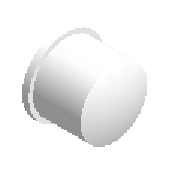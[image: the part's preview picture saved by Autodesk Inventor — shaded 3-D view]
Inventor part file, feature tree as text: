
AUTODESK INVENTOR PART (.ipt)
format: ipt  version: 2023.1 (Build 271208000, 208)  size: 160,256 bytes
history: native  units: mm (DEFAULTED — no unit token found)
features: other x4, revolve x2, sketch x1
ambient origin geometry x8: Origin, YZ Plane, XZ Plane, XY Plane, X Axis, Y Axis, Z Axis, Center Point
bodies: Solid1 (feature_tree)
feature tree (7):
  sketch  "Sketch1"  dims[d1=25.0mm d0=2.85mm d2=1.9mm d3=1.9mm d4=25.0mm d5=19.0mm d6=3.8mm d7=90.0deg d8=90.0deg]
  revolve  "Revolve1"  [1 undecoded]
  revolve  "Revolve2"  [1 undecoded]
  other  "Work Point1"
  other  "Work Axis1"
  other  "Work Point2"
  other  "Work Point3"
note: 2 required parameter values undecoded (feature->parameter linkage not recoverable at this tier; creation-order binding heuristic only, values carry confidence <= 0.55)
